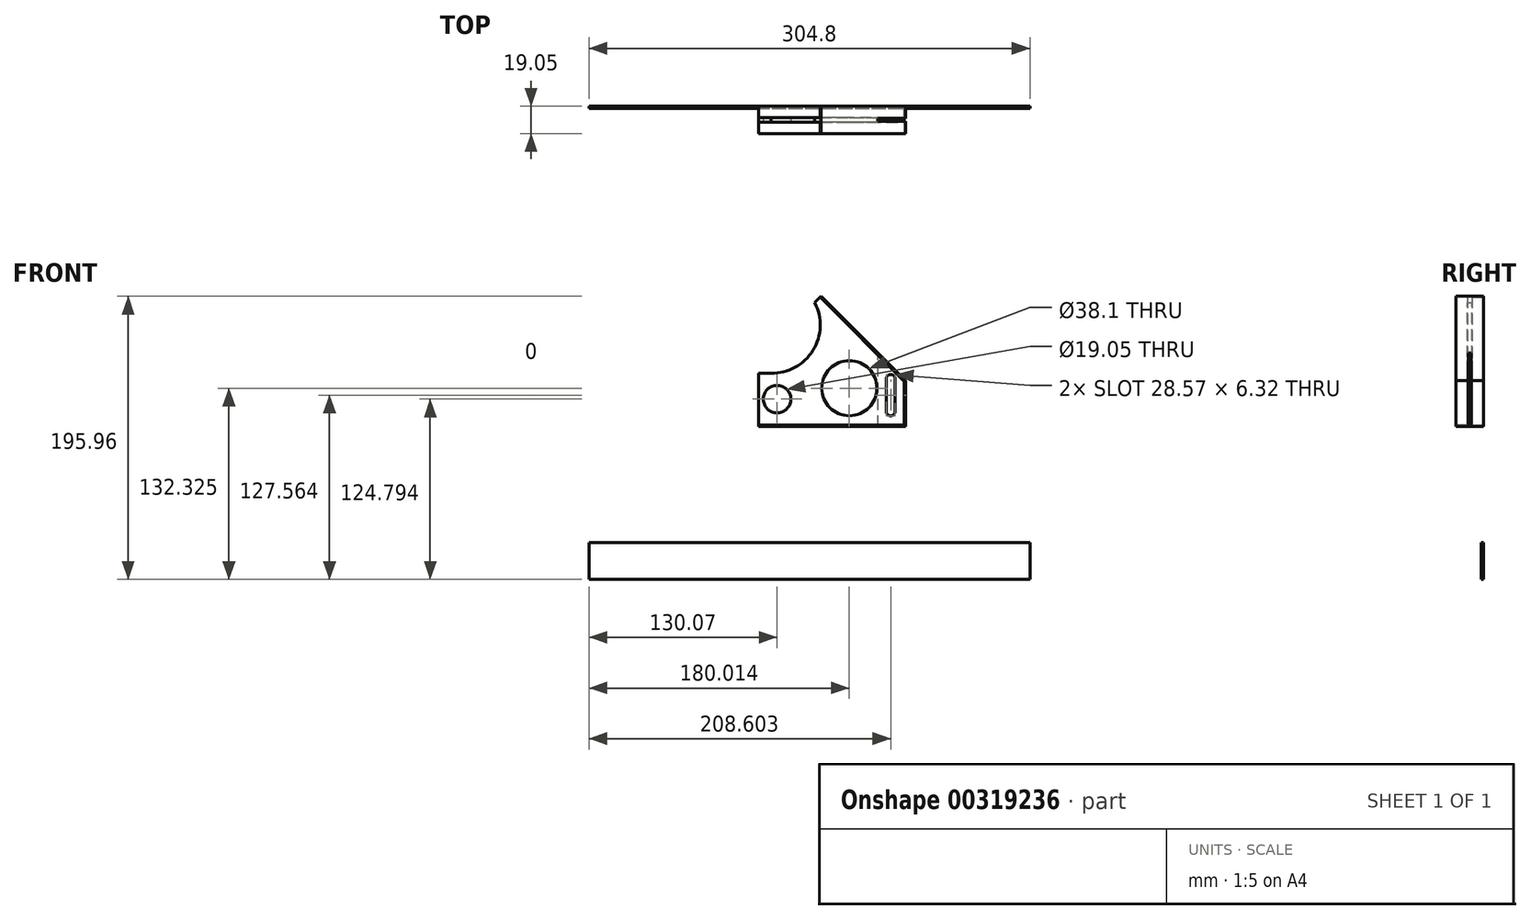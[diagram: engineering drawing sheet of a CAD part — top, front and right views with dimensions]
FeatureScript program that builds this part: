
annotation { "Feature Type Name" : "Feature", "Feature Type Description" : "" }
export const myFeature = defineFeature(function(context is Context, id is Id, definition is map)
    precondition{}
    {
        {
            var Q0;
            Q0=qCreatedBy(makeId("Front.planeOp"),FACE);
            var sketch = newSketch(context, id + "F0", { "sketchPlane" : qUnion([Q0])});
            skLineSegment(sketch, "E0", {"start": v(-1364.8, -160.44) * mm, "end": v(-1060, -160.44) * mm});
            skLineSegment(sketch, "E1", {"start": v(-1060, -160.44) * mm, "end": v(-1060, -135.04) * mm});
            skLineSegment(sketch, "E2", {"start": v(-1364.8, -160.44) * mm, "end": v(-1364.8, -135.04) * mm});
            skLineSegment(sketch, "E3", {"start": v(-1364.8, -135.04) * mm, "end": v(-1060, -135.04) * mm});
            skSolve(sketch);
        }
        {
            var Q0;
            Q0=makeQuery(id+"F0.imprint","IMPRINT",FACE,{"disambiguationData":[TD([[makeQuery(id+"F0.imprint","IMPRINT",EDGE,{"derivedFrom":sQuery(id+"F0.wireOp",EDGE,"E0")}),1.0]])]});
            extrude(context, id + "F1", {"entities" : qUnion([Q0]), "depth" : 1.59 * mm});
        }
        {
            var Q0;
            Q0=qCreatedBy(makeId("Front.planeOp"),FACE);
            var sketch = newSketch(context, id + "F2", { "sketchPlane" : qUnion([Q0])});
            skLineSegment(sketch, "E4", {"start": v(-1145.83, -54.6) * mm, "end": v(-1247.43, -54.6) * mm});
            skLineSegment(sketch, "E5", {"start": v(-1145.83, -54.6) * mm, "end": v(-1145.83, -22.85) * mm});
            skLineSegment(sketch, "E6", {"start": v(-1247.43, -54.6) * mm, "end": v(-1202.98, -54.6) * mm});
            skLineSegment(sketch, "E7", {"start": v(-1204.2, 35.52) * mm, "end": v(-1145.83, -22.85) * mm});
            skLineSegment(sketch, "E8", {"start": v(-1204.2, 35.52) * mm, "end": v(-1208.7, 31.03) * mm});
            skLineSegment(sketch, "E9", {"start": v(-1247.43, -54.6) * mm, "end": v(-1247.43, -17.78) * mm});
            skArc(sketch, "E10", {"start": v(-1238.8, -17.78) * mm, "mid": v(-1209.87, -1.93) * mm, "end": v(-1208.7, 31.03) * mm});
            skPoint(sketch, "E10.third.point", {"position": v(-1215.88, -9.16) * mm});
            skLineSegment(sketch, "E11", {"start": v(-1237.74, -17.78) * mm, "end": v(-1247.43, -17.78) * mm});
            skSolve(sketch);
        }
        {
            var Q0;
            Q0=makeQuery(id+"F2.imprint","IMPRINT",FACE,{"disambiguationData":[TD([[makeQuery(id+"F2.imprint","IMPRINT",EDGE,{"derivedFrom":sQuery(id+"F2.wireOp",EDGE,"E4")}),-1.0]])]});
            extrude(context, id + "F3", {"entities" : qUnion([Q0]), "depth" : 19.05 * mm});
        }
        {
            var Q0;
            Q0=makeQuery(id+"F3.opExtrude","CAP_FACE",FACE,{"disambiguationData":[OSD([sQuery(id+"F2.wireOp",EDGE,"E4"),sQuery(id+"F2.wireOp",EDGE,"E5"),sQuery(id+"F2.wireOp",EDGE,"E6"),sQuery(id+"F2.wireOp",EDGE,"E7"),sQuery(id+"F2.wireOp",EDGE,"E8"),sQuery(id+"F2.wireOp",EDGE,"E9"),sQuery(id+"F2.wireOp",EDGE,"E10"),sQuery(id+"F2.wireOp",EDGE,"E11")])],"isStart":false});
            var sketch = newSketch(context, id + "F4", { "sketchPlane" : qUnion([Q0])});
            skLineSegment(sketch, "E12", {"start": v(-1204.2, 35.52) * mm, "end": v(-1204.88, 34.85) * mm});
            skLineSegment(sketch, "E13", {"start": v(-1204.88, 34.85) * mm, "end": v(-1146.69, -23.34) * mm});
            skLineSegment(sketch, "E14", {"start": v(-1146.69, -23.34) * mm, "end": v(-1146.69, -53.52) * mm});
            skLineSegment(sketch, "E15", {"start": v(-1146.69, -53.52) * mm, "end": v(-1245.99, -53.52) * mm});
            skLineSegment(sketch, "E16", {"start": v(-1245.99, -53.52) * mm, "end": v(-1247.43, -53.52) * mm});
            skSolve(sketch);
        }
        {
            var Q0;
            {var subQ1=sQuery(id+"F4.wireOp",EDGE,"E13");Q0=makeQuery(id+"F4.imprint","IMPRINT",FACE,{"disambiguationData":[TD([[makeQuery(id+"F4.imprint","IMPRINT",EDGE,{"derivedFrom":subQ1}),-1.0]])]});}
            extrude(context, id + "F5", {"entities" : qUnion([Q0]), "operationType" : NewBodyOperationType.REMOVE, "oppositeDirection" : true, "depth" : 7.94 * mm});
        }
        {
            var Q0;
            Q0=makeQuery(id+"F3.opExtrude","CAP_FACE",FACE,{"disambiguationData":[OSD([sQuery(id+"F2.wireOp",EDGE,"E4"),sQuery(id+"F2.wireOp",EDGE,"E5"),sQuery(id+"F2.wireOp",EDGE,"E6"),sQuery(id+"F2.wireOp",EDGE,"E7"),sQuery(id+"F2.wireOp",EDGE,"E8"),sQuery(id+"F2.wireOp",EDGE,"E9"),sQuery(id+"F2.wireOp",EDGE,"E10"),sQuery(id+"F2.wireOp",EDGE,"E11")])],"isStart":true});
            var sketch = newSketch(context, id + "F6", { "sketchPlane" : qUnion([Q0])});
            skLineSegment(sketch, "E17", {"start": v(1204.2, 35.52) * mm, "end": v(1204.88, 34.85) * mm});
            skLineSegment(sketch, "E18", {"start": v(1204.88, 34.85) * mm, "end": v(1146.83, -23.2) * mm});
            skLineSegment(sketch, "E19", {"start": v(1146.83, -23.2) * mm, "end": v(1146.83, -53.47) * mm});
            skLineSegment(sketch, "E20", {"start": v(1146.83, -53.47) * mm, "end": v(1247.43, -53.47) * mm});
            skSolve(sketch);
        }
        {
            var Q0;
            Q0=makeQuery(id+"F5.boolean.opBoolean","COPY",FACE,{"derivedFrom":makeQuery(id+"F5.opExtrude","CAP_FACE",FACE,{"disambiguationData":[OSD([sQuery(id+"F2.wireOp",EDGE,"E8"),sQuery(id+"F2.wireOp",EDGE,"E9"),sQuery(id+"F2.wireOp",EDGE,"E10"),sQuery(id+"F2.wireOp",EDGE,"E11"),sQuery(id+"F4.wireOp",EDGE,"E13"),sQuery(id+"F4.wireOp",EDGE,"E14"),sQuery(id+"F4.wireOp",EDGE,"E15"),sQuery(id+"F4.wireOp",EDGE,"E16")])],"isStart":false})});
            var sketch = newSketch(context, id + "F7", { "sketchPlane" : qUnion([Q0])});
            skLineSegment(sketch, "E21", {"start": v(-1146.69, -53.52) * mm, "end": v(-1146.69, -28.12) * mm});
            skLineSegment(sketch, "E22", {"start": v(-1146.69, -28.12) * mm, "end": v(-1184.79, -28.12) * mm});
            skSolve(sketch);
        }
        {
            var Q0;
            Q0 = qSketchRegion(id + "F6", true);
            var Q1;
            {var subQ3=sQuery(id+"F6.wireOp",EDGE,"E18");Q1=makeQuery(id+"F6.imprint","IMPRINT",FACE,{"disambiguationData":[TD([[makeQuery(id+"F6.imprint","IMPRINT",EDGE,{"derivedFrom":subQ3}),1.0]])]});}
            extrude(context, id + "F8", {"entities" : qUnion([Q0, Q1]), "operationType" : NewBodyOperationType.REMOVE, "oppositeDirection" : true, "depth" : 7.94 * mm});
        }
        {
            var Q0;
            Q0=sQuery(id+"F7.wireOp",VERTEX,"E22.end");
            var Q1;
            Q1=makeQuery(id+"F3.opExtrude","SWEPT_BODY",BODY,{"disambiguationData":[OSD([sQuery(id+"F2.wireOp",EDGE,"E4"),sQuery(id+"F2.wireOp",EDGE,"E5"),sQuery(id+"F2.wireOp",EDGE,"E6"),sQuery(id+"F2.wireOp",EDGE,"E7"),sQuery(id+"F2.wireOp",EDGE,"E8"),sQuery(id+"F2.wireOp",EDGE,"E9"),sQuery(id+"F2.wireOp",EDGE,"E10"),sQuery(id+"F2.wireOp",EDGE,"E11")])]});
            hole(context, id + "F9", {"style" : HoleStyle.SIMPLE, "endStyle" : HoleEndStyle.THROUGH, "holeDiameter" : 38.1 * mm, "tappedDepth" : 12.7 * mm, "tapClearance" : 3, "locations" : qUnion([Q0]), "scope" : qUnion([Q1])});
        }
        {
            var Q0;
            Q0=makeQuery(id+"F5.boolean.opBoolean","COPY",FACE,{"derivedFrom":makeQuery(id+"F5.opExtrude","CAP_FACE",FACE,{"disambiguationData":[OSD([sQuery(id+"F2.wireOp",EDGE,"E8"),sQuery(id+"F2.wireOp",EDGE,"E9"),sQuery(id+"F2.wireOp",EDGE,"E10"),sQuery(id+"F2.wireOp",EDGE,"E11"),sQuery(id+"F4.wireOp",EDGE,"E13"),sQuery(id+"F4.wireOp",EDGE,"E14"),sQuery(id+"F4.wireOp",EDGE,"E15"),sQuery(id+"F4.wireOp",EDGE,"E16")])],"isStart":false})});
            var sketch = newSketch(context, id + "F10", { "sketchPlane" : qUnion([Q0])});
            skLineSegment(sketch, "E23", {"start": v(-1247.43, -35.65) * mm, "end": v(-1234.73, -35.65) * mm});
            skSolve(sketch);
        }
        {
            var Q0;
            Q0=sQuery(id+"F10.wireOp",VERTEX,"E23.end");
            var Q1;
            Q1=makeQuery(id+"F3.opExtrude","SWEPT_BODY",BODY,{"disambiguationData":[OSD([sQuery(id+"F2.wireOp",EDGE,"E4"),sQuery(id+"F2.wireOp",EDGE,"E5"),sQuery(id+"F2.wireOp",EDGE,"E6"),sQuery(id+"F2.wireOp",EDGE,"E7"),sQuery(id+"F2.wireOp",EDGE,"E8"),sQuery(id+"F2.wireOp",EDGE,"E9"),sQuery(id+"F2.wireOp",EDGE,"E10"),sQuery(id+"F2.wireOp",EDGE,"E11")])]});
            hole(context, id + "F11", {"style" : HoleStyle.SIMPLE, "endStyle" : HoleEndStyle.THROUGH, "holeDiameter" : 19.05 * mm, "tappedDepth" : 12.7 * mm, "tapClearance" : 3, "locations" : qUnion([Q0]), "scope" : qUnion([Q1])});
        }
        {
            var Q0;
            Q0=makeQuery(id+"F5.boolean.opBoolean","COPY",FACE,{"derivedFrom":makeQuery(id+"F5.opExtrude","CAP_FACE",FACE,{"disambiguationData":[OSD([sQuery(id+"F2.wireOp",EDGE,"E8"),sQuery(id+"F2.wireOp",EDGE,"E9"),sQuery(id+"F2.wireOp",EDGE,"E10"),sQuery(id+"F2.wireOp",EDGE,"E11"),sQuery(id+"F4.wireOp",EDGE,"E13"),sQuery(id+"F4.wireOp",EDGE,"E14"),sQuery(id+"F4.wireOp",EDGE,"E15"),sQuery(id+"F4.wireOp",EDGE,"E16")])],"isStart":false})});
            var sketch = newSketch(context, id + "F12", { "sketchPlane" : qUnion([Q0])});
            skLineSegment(sketch, "E24", {"start": v(-1146.69, -53.52) * mm, "end": v(-1156.21, -53.52) * mm});
            skArc(sketch, "E25", {"start": v(-1159.36, -43.57) * mm, "mid": v(-1156.42, -47.16) * mm, "end": v(-1153.04, -43.99) * mm});
            skArc(sketch, "E26", {"start": v(-1153.04, -21.9) * mm, "mid": v(-1156.35, -18.6) * mm, "end": v(-1159.36, -22.18) * mm});
            skLineSegment(sketch, "E27", {"start": v(-1153.04, -21.63) * mm, "end": v(-1153.04, -43.99) * mm});
            skLineSegment(sketch, "E28", {"start": v(-1159.36, -21.35) * mm, "end": v(-1159.36, -44.4) * mm});
            skSolve(sketch);
        }
        {
            var Q0;
            {var subQ0=sQuery(id+"F12.wireOp",EDGE,"E27");var subQ6=sQuery(id+"F12.wireOp",EDGE,"E25");var subQ7=makeQuery(id+"F12.imprint","INTERSECT",VERTEX,{"derivedFrom":[subQ6,subQ0]});Q0=makeQuery(id+"F12.imprint","IMPRINT",FACE,{"disambiguationData":[TD([[makeQuery(id+"F12.imprint","IMPRINT",EDGE,{"disambiguationData":[TD([[subQ7,1.0]])],"derivedFrom":subQ6}),1.0]])]});}
            extrude(context, id + "F13", {"entities" : qUnion([Q0]), "operationType" : NewBodyOperationType.REMOVE, "endBound" : BoundingType.THROUGH_ALL, "oppositeDirection" : true, "depth" : 0 * mm});
        }
        {
            var Q0;
            Q0=makeQuery(id+"F3.opExtrude","SWEPT_FACE",FACE,{"disambiguationData":[OSD([sQuery(id+"F2.wireOp",EDGE,"E5")])]});
            var sketch = newSketch(context, id + "F14", { "sketchPlane" : qUnion([Q0])});
            skPoint(sketch, "E29.endSnap0", {"position": v(-9.53, -22.85) * mm});
            skLineSegment(sketch, "E30", {"start": v(-9.53, -54.6) * mm, "end": v(-10.48, -54.6) * mm});
            skLineSegment(sketch, "E31", {"start": v(-9.53, -54.6) * mm, "end": v(-8.57, -54.6) * mm});
            skLineSegment(sketch, "E32", {"start": v(-10.48, -54.6) * mm, "end": v(-10.48, -3.8) * mm});
            skLineSegment(sketch, "E33", {"start": v(-10.48, -3.8) * mm, "end": v(-9.53, -3.8) * mm});
            skLineSegment(sketch, "E34", {"start": v(-8.57, -54.6) * mm, "end": v(-8.57, -3.8) * mm});
            skLineSegment(sketch, "E35", {"start": v(-8.57, -3.8) * mm, "end": v(-9.53, -3.8) * mm});
            skSolve(sketch);
        }
        {
            var Q0;
            {var subQ1=sQuery(id+"F14.wireOp",EDGE,"E30");Q0=makeQuery(id+"F14.imprint","IMPRINT",FACE,{"disambiguationData":[TD([[makeQuery(id+"F14.imprint","IMPRINT",EDGE,{"derivedFrom":subQ1}),1.0]])]});}
            var Q1;
            {var subQ4=sQuery(id+"F14.wireOp",EDGE,"E33");Q1=makeQuery(id+"F14.imprint","IMPRINT",FACE,{"disambiguationData":[TD([[makeQuery(id+"F14.imprint","IMPRINT",EDGE,{"derivedFrom":subQ4}),-1.0]])]});}
            extrude(context, id + "F15", {"entities" : qUnion([Q0, Q1]), "operationType" : NewBodyOperationType.REMOVE, "oppositeDirection" : true, "depth" : 19.05 * mm});
        }
    });
